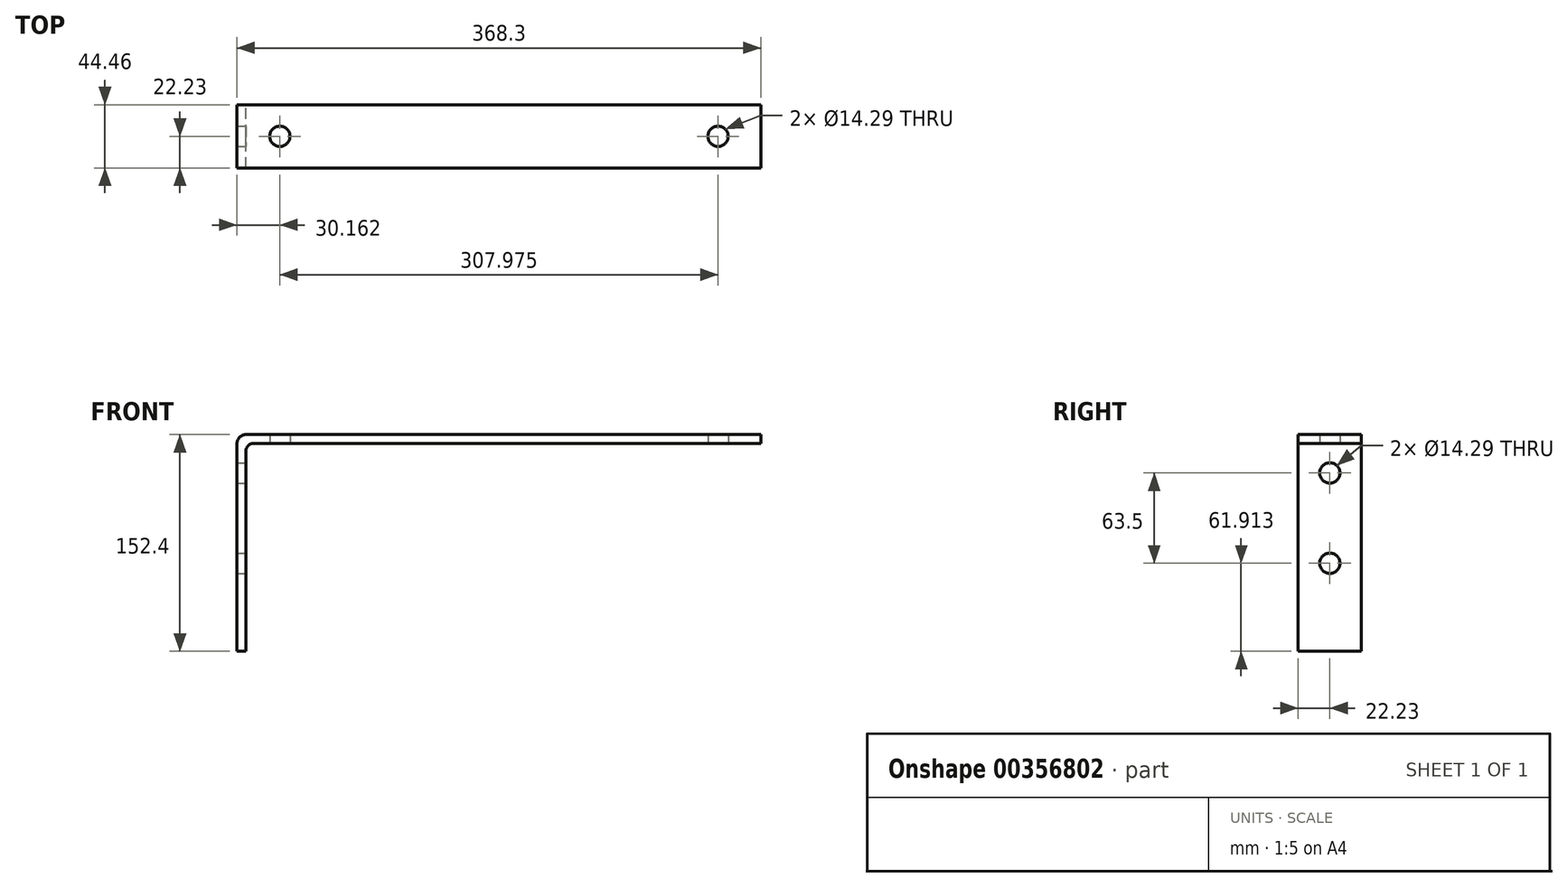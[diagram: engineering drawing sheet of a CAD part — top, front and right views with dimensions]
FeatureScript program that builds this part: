
annotation { "Feature Type Name" : "Feature", "Feature Type Description" : "" }
export const myFeature = defineFeature(function(context is Context, id is Id, definition is map)
    precondition{}
    {
        {
            var Q0;
            Q0=qCreatedBy(makeId("Front.planeOp"),FACE);
            var sketch = newSketch(context, id + "F0", { "sketchPlane" : qUnion([Q0])});
            skLineSegment(sketch, "E0", {"start": v(-76.3, 0) * mm, "end": v(-76.3, 152.4) * mm});
            skLineSegment(sketch, "E1", {"start": v(-76.3, 152.4) * mm, "end": v(292, 152.4) * mm});
            skLineSegment(sketch, "E2", {"start": v(292, 152.4) * mm, "end": v(292, 146.05) * mm});
            skLineSegment(sketch, "E3", {"start": v(292, 146.05) * mm, "end": v(-69.95, 146.05) * mm});
            skLineSegment(sketch, "E4", {"start": v(-69.95, 146.05) * mm, "end": v(-69.95, 0) * mm});
            skLineSegment(sketch, "E5", {"start": v(-69.95, 0) * mm, "end": v(-76.3, 0) * mm});
            skSolve(sketch);
        }
        {
            var Q0;
            Q0 = qSketchRegion(id + "F0", true);
            extrude(context, id + "F1", {"entities" : qUnion([Q0]), "endBound" : BoundingType.SYMMETRIC, "depth" : 44.45 * mm});
        }
        {
            var Q0;
            Q0=makeQuery(id+"F1.opExtrude","SWEPT_EDGE",EDGE,{"disambiguationData":[OSD([sQuery(id+"F0.wireOp",EDGE,"E3"),sQuery(id+"F0.wireOp",EDGE,"E4")])]});
            fillet(context, id + "F2", {"entities" : qUnion([Q0]), "radius" : 5.08 * mm, "tangentPropagation" : true, "allowEdgeOverflow" : false});
        }
        {
            var Q0;
            Q0=makeQuery(id+"F1.opExtrude","SWEPT_EDGE",EDGE,{"disambiguationData":[OSD([sQuery(id+"F0.wireOp",EDGE,"E0"),sQuery(id+"F0.wireOp",EDGE,"E1")])]});
            fillet(context, id + "F3", {"entities" : qUnion([Q0]), "radius" : 6.35 * mm, "tangentPropagation" : true, "allowEdgeOverflow" : false});
        }
        {
            var Q0;
            Q0=qCreatedBy(makeId("Top.planeOp"),FACE);
            var sketch = newSketch(context, id + "F4", { "sketchPlane" : qUnion([Q0])});
            skCircle(sketch, "E6", {"center": v(261.84, 0) * mm, "radius": 7.14 * mm});
            skCircle(sketch, "E7", {"center": v(-46.14, 0) * mm, "radius": 7.14 * mm});
            skSolve(sketch);
        }
        {
            var Q0;
            Q0 = qSketchRegion(id + "F4", true);
            extrude(context, id + "F5", {"entities" : qUnion([Q0]), "operationType" : NewBodyOperationType.REMOVE, "endBound" : BoundingType.THROUGH_ALL, "depth" : 25.4 * mm});
        }
        {
            var Q0;
            Q0=qCreatedBy(makeId("Right.planeOp"),FACE);
            var sketch = newSketch(context, id + "F6", { "sketchPlane" : qUnion([Q0])});
            skCircle(sketch, "E8", {"center": v(0, 125.41) * mm, "radius": 7.14 * mm});
            skPoint(sketch, "E9.0", {"position": v(22.23, 152.4) * mm});
            skLineSegment(sketch, "E10", {"start": v(22.23, 152.4) * mm, "end": v(-22.25, 152.4) * mm});
            skLineSegment(sketch, "E11", {"start": v(-22.25, 152.4) * mm, "end": v(-28.35, 150.43) * mm});
            skCircle(sketch, "E12", {"center": v(0, 61.91) * mm, "radius": 7.14 * mm});
            skSolve(sketch);
        }
        {
            var Q0;
            Q0 = qSketchRegion(id + "F6", true);
            extrude(context, id + "F7", {"entities" : qUnion([Q0]), "operationType" : NewBodyOperationType.REMOVE, "endBound" : BoundingType.THROUGH_ALL, "oppositeDirection" : true, "depth" : 25.4 * mm});
        }
    });
